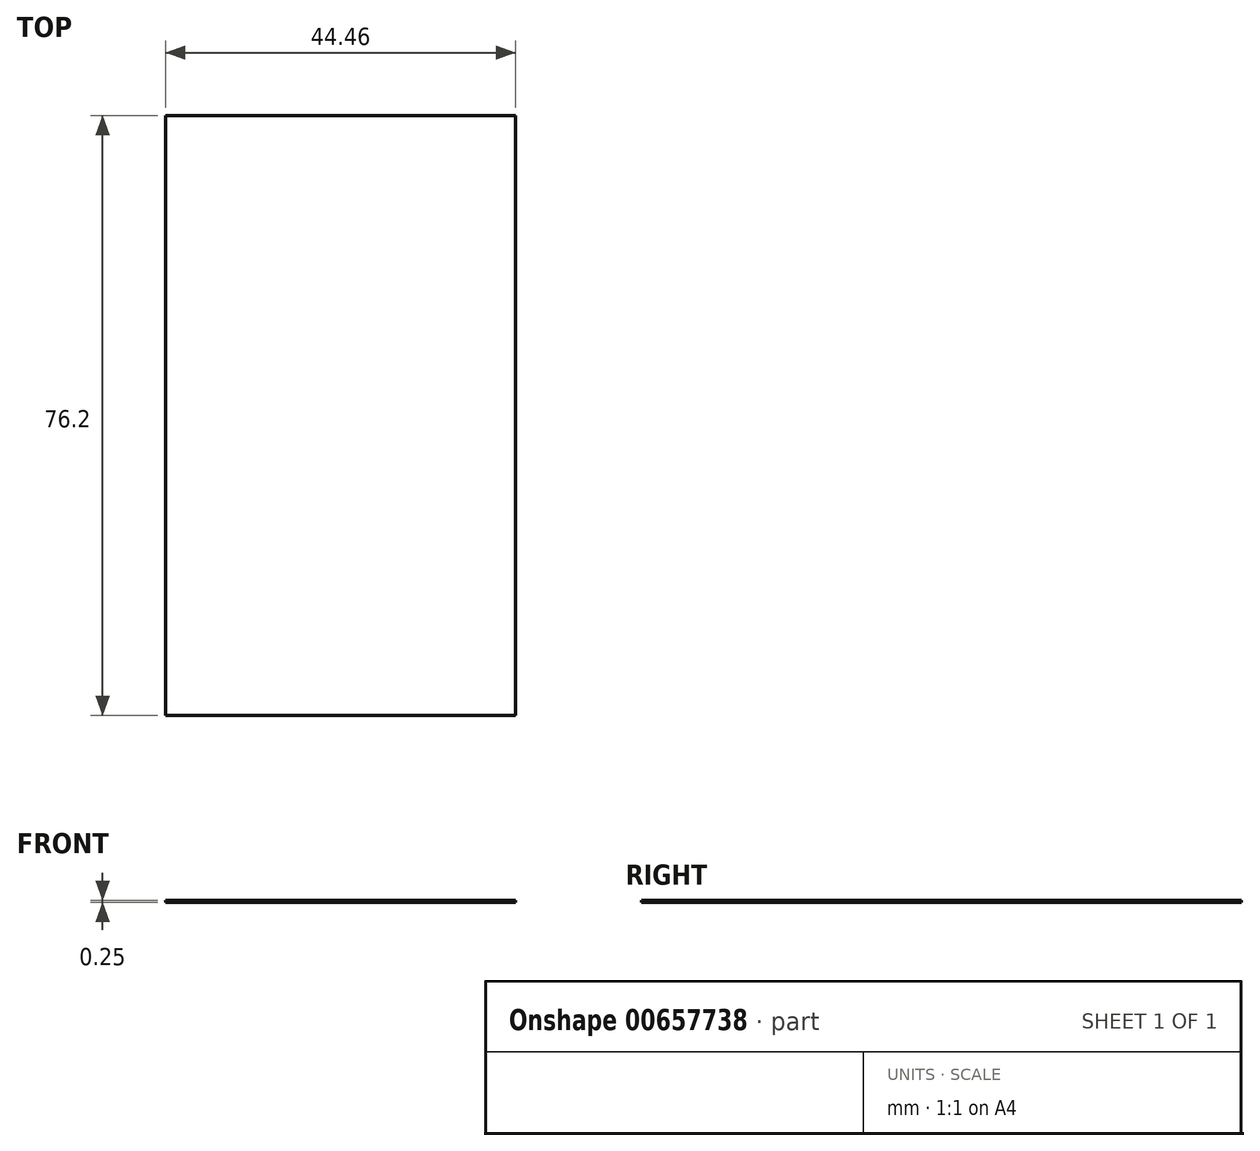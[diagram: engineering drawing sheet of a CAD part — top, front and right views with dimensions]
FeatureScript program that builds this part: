
annotation { "Feature Type Name" : "Feature", "Feature Type Description" : "" }
export const myFeature = defineFeature(function(context is Context, id is Id, definition is map)
    precondition{}
    {
        {
            var Q0;
            Q0=qCreatedBy(makeId("Top.planeOp"),FACE);
            var sketch = newSketch(context, id + "F0", { "sketchPlane" : qUnion([Q0])});
            skLineSegment(sketch, "E0.bottom", {"start": v(22.23, 38.1) * mm, "end": v(-22.23, 38.1) * mm});
            skLineSegment(sketch, "E0.top", {"start": v(22.23, -38.1) * mm, "end": v(-22.23, -38.1) * mm});
            skLineSegment(sketch, "E0.left", {"start": v(22.23, 38.1) * mm, "end": v(22.22, -38.1) * mm});
            skLineSegment(sketch, "E0.right", {"start": v(-22.23, 38.1) * mm, "end": v(-22.23, -38.1) * mm});
            skPoint(sketch, "E0.middle", {"position": v(0, 0) * mm});
            skSolve(sketch);
        }
        {
            var Q0;
            Q0=makeQuery(id+"F0.imprint","IMPRINT",FACE,{"disambiguationData":[TD([[makeQuery(id+"F0.imprint","IMPRINT",EDGE,{"derivedFrom":sQuery(id+"F0.wireOp",EDGE,"E0.bottom")}),1.0]])]});
            extrude(context, id + "F1", {"entities" : qUnion([Q0]), "depth" : 0.25 * mm, "offsetDistance" : 25.4 * mm});
        }
    });
